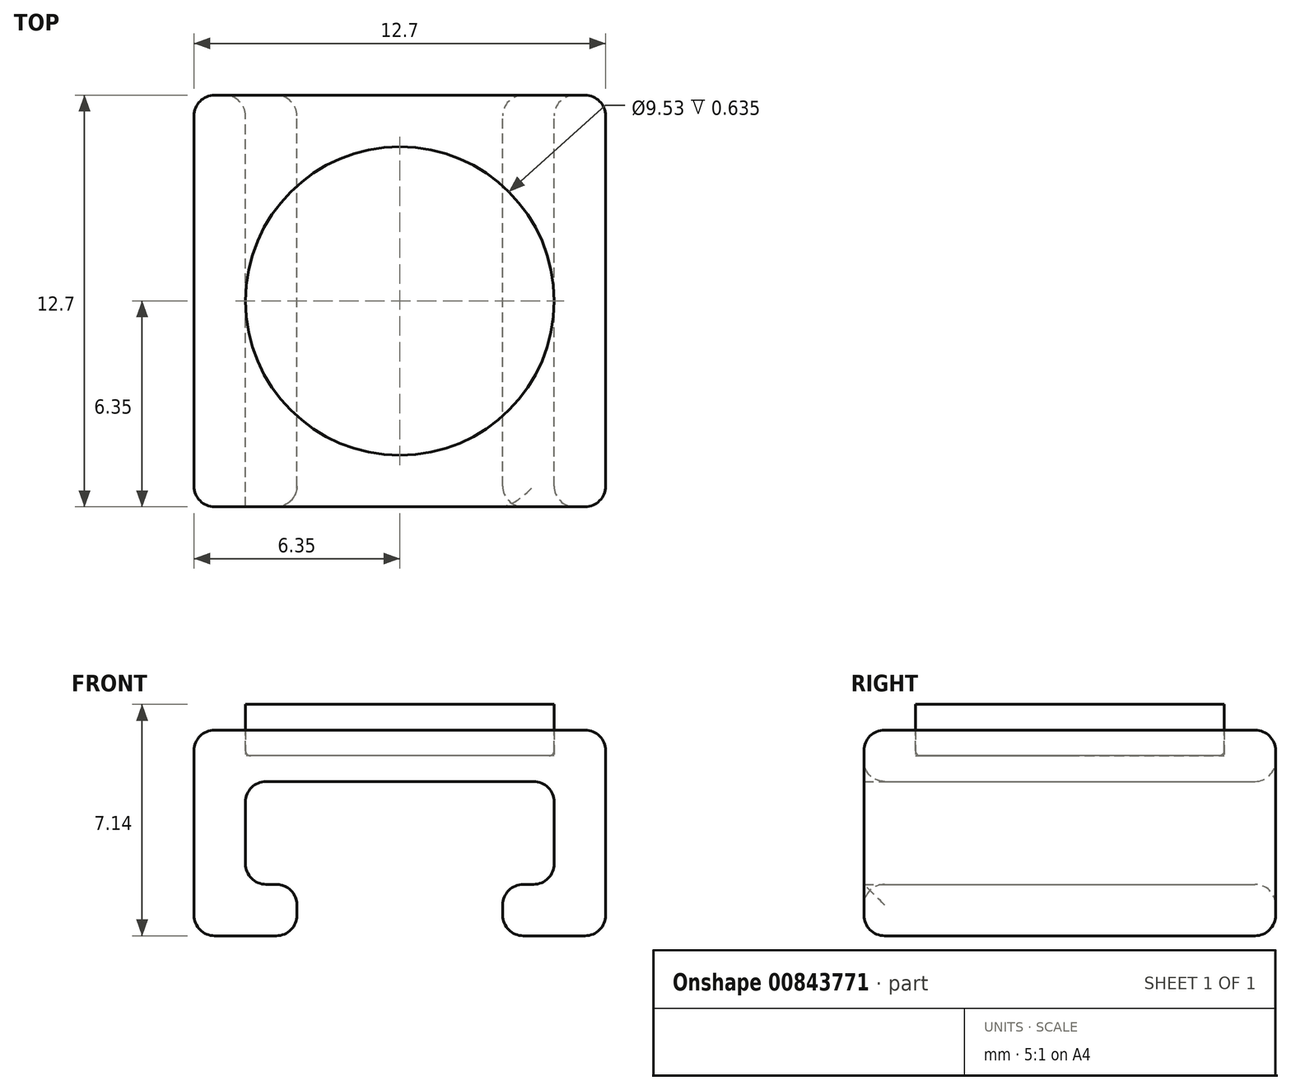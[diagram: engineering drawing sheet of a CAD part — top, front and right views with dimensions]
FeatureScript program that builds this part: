
annotation { "Feature Type Name" : "Feature", "Feature Type Description" : "" }
export const myFeature = defineFeature(function(context is Context, id is Id, definition is map)
    precondition{}
    {
        {
            var Q0;
            Q0=qCreatedBy(makeId("Front.planeOp"),FACE);
            var sketch = newSketch(context, id + "F0", { "sketchPlane" : qUnion([Q0])});
            skLineSegment(sketch, "E0", {"start": v(-6.35, 0) * mm, "end": v(6.35, 0) * mm});
            skLineSegment(sketch, "E1", {"start": v(-6.35, 0) * mm, "end": v(-6.35, -6.35) * mm});
            skLineSegment(sketch, "E2", {"start": v(-4.76, -4.76) * mm, "end": v(-4.76, -1.59) * mm});
            skLineSegment(sketch, "E3", {"start": v(-4.76, -1.59) * mm, "end": v(4.76, -1.59) * mm});
            skLineSegment(sketch, "E4", {"start": v(4.76, -1.59) * mm, "end": v(4.76, -4.76) * mm});
            skLineSegment(sketch, "E5", {"start": v(6.35, 0) * mm, "end": v(6.35, -6.35) * mm});
            skLineSegment(sketch, "E6", {"start": v(-4.76, -4.76) * mm, "end": v(-3.18, -4.76) * mm});
            skLineSegment(sketch, "E7", {"start": v(-3.18, -4.76) * mm, "end": v(-3.18, -6.35) * mm});
            skLineSegment(sketch, "E8", {"start": v(4.76, -4.76) * mm, "end": v(3.17, -4.76) * mm});
            skLineSegment(sketch, "E9", {"start": v(3.17, -4.76) * mm, "end": v(3.17, -6.35) * mm});
            skLineSegment(sketch, "E10", {"start": v(-6.35, -6.35) * mm, "end": v(-3.18, -6.35) * mm});
            skLineSegment(sketch, "E11", {"start": v(6.35, -6.35) * mm, "end": v(3.17, -6.35) * mm});
            skSolve(sketch);
        }
        {
            var Q0;
            Q0 = qSketchRegion(id + "F0", true);
            extrude(context, id + "F1", {"entities" : qUnion([Q0]), "depth" : 12.7 * mm, "offsetDistance" : 25.4 * mm});
        }
        {
            var Q0;
            Q0=makeQuery(id+"F1.opExtrude","SWEPT_FACE",FACE,{"disambiguationData":[OSD([sQuery(id+"F0.wireOp",EDGE,"E0")])]});
            var sketch = newSketch(context, id + "F2", { "sketchPlane" : qUnion([Q0])});
            skCircle(sketch, "E12", {"center": v(0, -6.35) * mm, "radius": 4.76 * mm});
            skSolve(sketch);
        }
        {
            var Q0;
            Q0=makeQuery(id+"F2.imprint","IMPRINT",FACE,{"disambiguationData":[TD([[makeQuery(id+"F2.imprint","IMPRINT",EDGE,{"derivedFrom":sQuery(id+"F2.wireOp",EDGE,"E12")}),1.0]])]});
            var Q1;
            Q1=sQuery(id+"F2.wireOp",EDGE,"E12");
            extrude(context, id + "F3", {"entities" : qUnion([Q0]), "operationType" : NewBodyOperationType.REMOVE, "surfaceEntities" : qUnion([Q1]), "oppositeDirection" : true, "depth" : 0.8 * mm, "offsetDistance" : 25.4 * mm});
        }
        {
            var Q0;
            Q0=makeQuery(id+"F1.opExtrude","CAP_EDGE",EDGE,{"disambiguationData":[OSD([sQuery(id+"F0.wireOp",EDGE,"E0")])],"isStart":true});
            var Q1;
            Q1=makeQuery(id+"F1.opExtrude","SWEPT_EDGE",EDGE,{"disambiguationData":[OSD([sQuery(id+"F0.wireOp",EDGE,"E0"),sQuery(id+"F0.wireOp",EDGE,"E1")])]});
            var Q2;
            Q2=makeQuery(id+"F1.opExtrude","CAP_EDGE",EDGE,{"disambiguationData":[OSD([sQuery(id+"F0.wireOp",EDGE,"E0")])],"isStart":false});
            var Q3;
            Q3=makeQuery(id+"F1.opExtrude","SWEPT_EDGE",EDGE,{"disambiguationData":[OSD([sQuery(id+"F0.wireOp",EDGE,"E0"),sQuery(id+"F0.wireOp",EDGE,"E5")])]});
            var Q4;
            Q4=makeQuery(id+"F1.opExtrude","CAP_EDGE",EDGE,{"disambiguationData":[OSD([sQuery(id+"F0.wireOp",EDGE,"E1")])],"isStart":true});
            var Q5;
            Q5=makeQuery(id+"F1.opExtrude","CAP_EDGE",EDGE,{"disambiguationData":[OSD([sQuery(id+"F0.wireOp",EDGE,"E1")])],"isStart":false});
            var Q6;
            Q6=makeQuery(id+"F1.opExtrude","CAP_EDGE",EDGE,{"disambiguationData":[OSD([sQuery(id+"F0.wireOp",EDGE,"E5")])],"isStart":true});
            var Q7;
            Q7=makeQuery(id+"F1.opExtrude","CAP_EDGE",EDGE,{"disambiguationData":[OSD([sQuery(id+"F0.wireOp",EDGE,"E5")])],"isStart":false});
            var Q8;
            Q8=makeQuery(id+"F1.opExtrude","SWEPT_EDGE",EDGE,{"disambiguationData":[OSD([sQuery(id+"F0.wireOp",EDGE,"E1"),sQuery(id+"F0.wireOp",EDGE,"E10")])]});
            var Q9;
            Q9=makeQuery(id+"F1.opExtrude","CAP_EDGE",EDGE,{"disambiguationData":[OSD([sQuery(id+"F0.wireOp",EDGE,"E10")])],"isStart":true});
            var Q10;
            Q10=makeQuery(id+"F1.opExtrude","SWEPT_EDGE",EDGE,{"disambiguationData":[OSD([sQuery(id+"F0.wireOp",EDGE,"E7"),sQuery(id+"F0.wireOp",EDGE,"E10")])]});
            var Q11;
            Q11=makeQuery(id+"F1.opExtrude","CAP_EDGE",EDGE,{"disambiguationData":[OSD([sQuery(id+"F0.wireOp",EDGE,"E10")])],"isStart":false});
            var Q12;
            Q12=makeQuery(id+"F1.opExtrude","CAP_EDGE",EDGE,{"disambiguationData":[OSD([sQuery(id+"F0.wireOp",EDGE,"E7")])],"isStart":true});
            var Q13;
            Q13=makeQuery(id+"F1.opExtrude","CAP_EDGE",EDGE,{"disambiguationData":[OSD([sQuery(id+"F0.wireOp",EDGE,"E7")])],"isStart":false});
            var Q14;
            Q14=makeQuery(id+"F1.opExtrude","CAP_EDGE",EDGE,{"disambiguationData":[OSD([sQuery(id+"F0.wireOp",EDGE,"E6")])],"isStart":true});
            var Q15;
            Q15=makeQuery(id+"F1.opExtrude","CAP_EDGE",EDGE,{"disambiguationData":[OSD([sQuery(id+"F0.wireOp",EDGE,"E2")])],"isStart":true});
            var Q16;
            Q16=makeQuery(id+"F1.opExtrude","CAP_EDGE",EDGE,{"disambiguationData":[OSD([sQuery(id+"F0.wireOp",EDGE,"E3")])],"isStart":true});
            var Q17;
            Q17=makeQuery(id+"F1.opExtrude","SWEPT_EDGE",EDGE,{"disambiguationData":[OSD([sQuery(id+"F0.wireOp",EDGE,"E6"),sQuery(id+"F0.wireOp",EDGE,"E7")])]});
            var Q18;
            Q18=makeQuery(id+"F1.opExtrude","SWEPT_EDGE",EDGE,{"disambiguationData":[OSD([sQuery(id+"F0.wireOp",EDGE,"E2"),sQuery(id+"F0.wireOp",EDGE,"E6")])]});
            var Q19;
            Q19=makeQuery(id+"F1.opExtrude","CAP_EDGE",EDGE,{"disambiguationData":[OSD([sQuery(id+"F0.wireOp",EDGE,"E9")])],"isStart":true});
            var Q20;
            Q20=makeQuery(id+"F1.opExtrude","CAP_EDGE",EDGE,{"disambiguationData":[OSD([sQuery(id+"F0.wireOp",EDGE,"E8")])],"isStart":true});
            var Q21;
            Q21=makeQuery(id+"F1.opExtrude","CAP_EDGE",EDGE,{"disambiguationData":[OSD([sQuery(id+"F0.wireOp",EDGE,"E4")])],"isStart":true});
            var Q22;
            Q22=makeQuery(id+"F1.opExtrude","CAP_EDGE",EDGE,{"disambiguationData":[OSD([sQuery(id+"F0.wireOp",EDGE,"E11")])],"isStart":true});
            var Q23;
            Q23=makeQuery(id+"F1.opExtrude","SWEPT_EDGE",EDGE,{"disambiguationData":[OSD([sQuery(id+"F0.wireOp",EDGE,"E2"),sQuery(id+"F0.wireOp",EDGE,"E3")])]});
            var Q24;
            Q24=makeQuery(id+"F1.opExtrude","SWEPT_EDGE",EDGE,{"disambiguationData":[OSD([sQuery(id+"F0.wireOp",EDGE,"E3"),sQuery(id+"F0.wireOp",EDGE,"E4")])]});
            var Q25;
            Q25=makeQuery(id+"F1.opExtrude","CAP_EDGE",EDGE,{"disambiguationData":[OSD([sQuery(id+"F0.wireOp",EDGE,"E4")])],"isStart":false});
            var Q26;
            Q26=makeQuery(id+"F1.opExtrude","SWEPT_EDGE",EDGE,{"disambiguationData":[OSD([sQuery(id+"F0.wireOp",EDGE,"E8"),sQuery(id+"F0.wireOp",EDGE,"E9")])]});
            var Q27;
            Q27=makeQuery(id+"F1.opExtrude","SWEPT_EDGE",EDGE,{"disambiguationData":[OSD([sQuery(id+"F0.wireOp",EDGE,"E9"),sQuery(id+"F0.wireOp",EDGE,"E11")])]});
            var Q28;
            Q28=makeQuery(id+"F1.opExtrude","SWEPT_EDGE",EDGE,{"disambiguationData":[OSD([sQuery(id+"F0.wireOp",EDGE,"E5"),sQuery(id+"F0.wireOp",EDGE,"E11")])]});
            var Q29;
            Q29=makeQuery(id+"F1.opExtrude","CAP_EDGE",EDGE,{"disambiguationData":[OSD([sQuery(id+"F0.wireOp",EDGE,"E8")])],"isStart":false});
            var Q30;
            Q30=makeQuery(id+"F1.opExtrude","CAP_EDGE",EDGE,{"disambiguationData":[OSD([sQuery(id+"F0.wireOp",EDGE,"E11")])],"isStart":false});
            var Q31;
            Q31=makeQuery(id+"F1.opExtrude","CAP_EDGE",EDGE,{"disambiguationData":[OSD([sQuery(id+"F0.wireOp",EDGE,"E9")])],"isStart":false});
            var Q32;
            Q32=makeQuery(id+"F1.opExtrude","SWEPT_EDGE",EDGE,{"disambiguationData":[OSD([sQuery(id+"F0.wireOp",EDGE,"E4"),sQuery(id+"F0.wireOp",EDGE,"E8")])]});
            fillet(context, id + "F4", {"entities" : qUnion([Q0, Q1, Q2, Q3, Q4, Q5, Q6, Q7, Q8, Q9, Q10, Q11, Q12, Q13, Q14, Q15, Q16, Q17, Q18, Q19, Q20, Q21, Q22, Q23, Q24, Q25, Q26, Q27, Q28, Q29, Q30, Q31, Q32]), "radius" : 0.64 * mm, "tangentPropagation" : true, "allowEdgeOverflow" : false});
        }
        {
            var Q0;
            Q0=makeQuery(id+"F3.boolean.opBoolean","COPY",EDGE,{"derivedFrom":makeQuery(id+"F3.opExtrude","CAP_EDGE",EDGE,{"disambiguationData":[OSD([sQuery(id+"F2.wireOp",EDGE,"E12")])],"isStart":true})});
            var Q1;
            Q1=makeQuery(id+"F3.boolean.opBoolean","COPY",EDGE,{"derivedFrom":makeQuery(id+"F3.opExtrude","CAP_EDGE",EDGE,{"disambiguationData":[OSD([sQuery(id+"F2.wireOp",EDGE,"E12")])],"isStart":false})});
            fillet(context, id + "F5", {"entities" : qUnion([Q0, Q1]), "radius" : 0.16 * mm, "tangentPropagation" : true, "allowEdgeOverflow" : false});
        }
        {
            var Q0;
            Q0=makeQuery(id+"F3.boolean.opBoolean","COPY",FACE,{"derivedFrom":makeQuery(id+"F3.opExtrude","CAP_FACE",FACE,{"disambiguationData":[OSD([sQuery(id+"F2.wireOp",EDGE,"E12")])],"isStart":false})});
            cPlane(context, id + "F6", {"entities" : qUnion([Q0]), "cplaneType" : CPlaneType.OFFSET, "offset" : 0 * mm, "width" : 152.4 * mm, "height" : 152.4 * mm});
        }
        {
            var Q0;
            Q0=qCreatedBy(id+"F6.planeOp",FACE);
            var sketch = newSketch(context, id + "F7", { "sketchPlane" : qUnion([Q0])});
            skCircle(sketch, "E13.0", {"center": v(0, -6.35) * mm, "radius": 4.76 * mm});
            skSolve(sketch);
        }
        {
            var Q0;
            Q0 = qSketchRegion(id + "F7", true);
            extrude(context, id + "F8", {"entities" : qUnion([Q0]), "depth" : 1.59 * mm, "offsetDistance" : 25.4 * mm});
        }
    });
